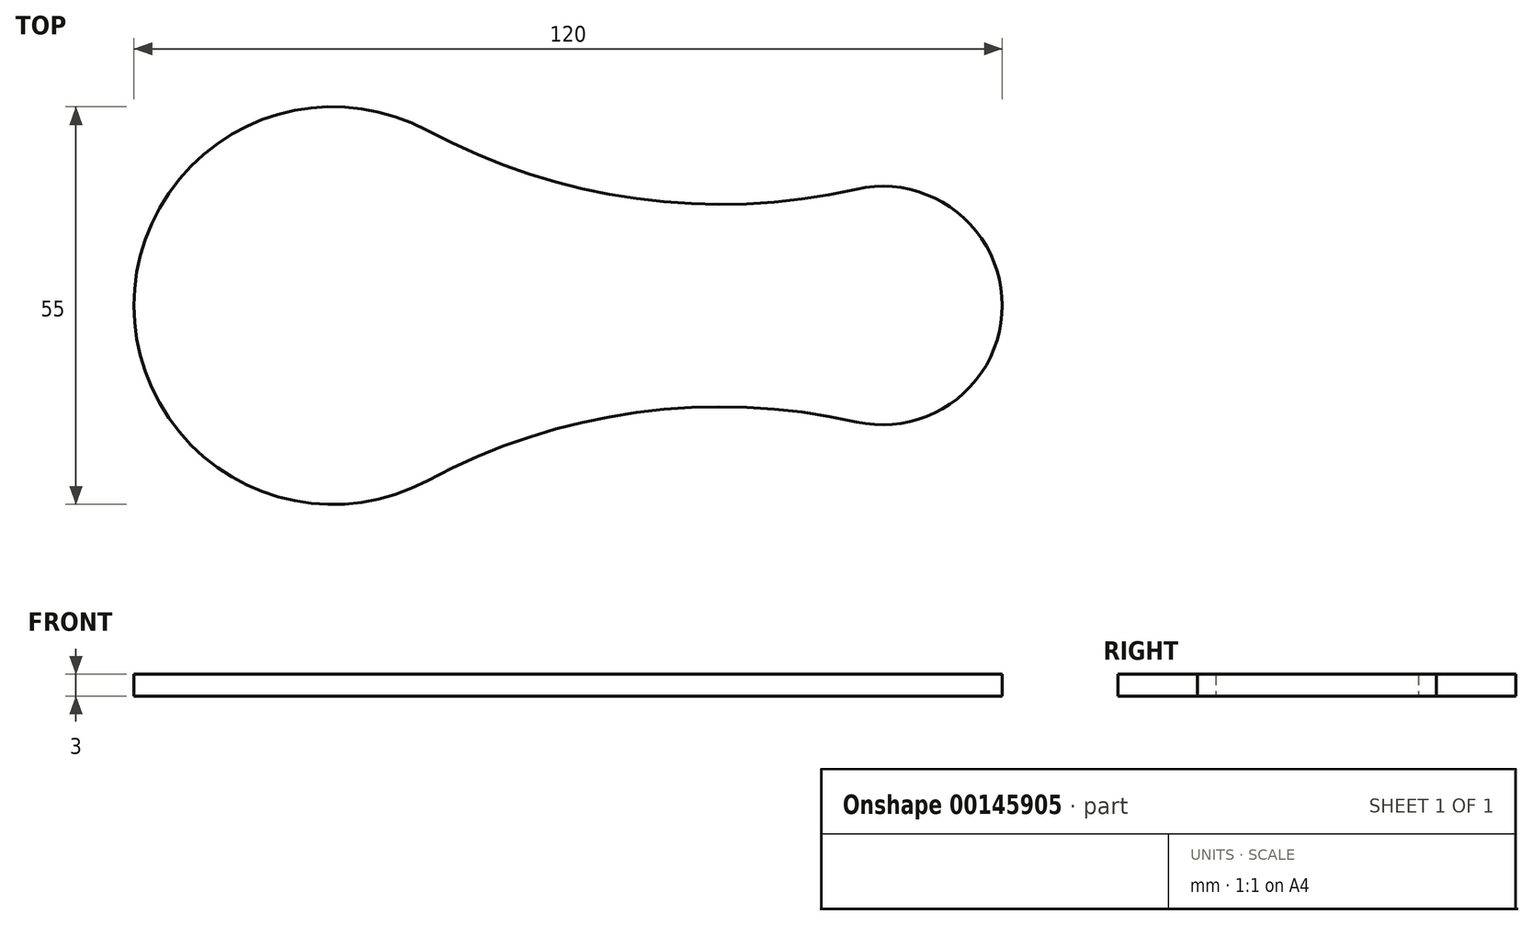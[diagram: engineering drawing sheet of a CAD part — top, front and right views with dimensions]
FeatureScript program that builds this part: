
annotation { "Feature Type Name" : "Feature", "Feature Type Description" : "" }
export const myFeature = defineFeature(function(context is Context, id is Id, definition is map)
    precondition{}
    {
        {
            var Q0;
            Q0=qCreatedBy(makeId("Top.planeOp"),FACE);
            var sketch = newSketch(context, id + "F0", { "sketchPlane" : qUnion([Q0])});
            skArc(sketch, "E0", {"start": v(72.37, 16.1) * mm, "mid": v(86.3, 12.89) * mm, "end": v(92.5, 0) * mm});
            skArc(sketch, "E1", {"start": v(13.04, 24.21) * mm, "mid": v(-14.1, 23.6) * mm, "end": v(-27.5, 0) * mm});
            skLineSegment(sketch, "E2", {"start": v(-27.5, 0) * mm, "end": v(92.5, 0) * mm, "construction": true});
            skArc(sketch, "E3", {"start": v(13.04, 24.21) * mm, "mid": v(41.97, 14.79) * mm, "end": v(72.37, 16.1) * mm});
            skArc(sketch, "E4.0", {"start": v(71.27, 20.97) * mm, "mid": v(89.43, 16.8) * mm, "end": v(97.5, 0) * mm});
            skArc(sketch, "E4.1", {"start": v(15.4, 28.62) * mm, "mid": v(42.65, 19.74) * mm, "end": v(71.27, 20.97) * mm});
            skArc(sketch, "E4.2", {"start": v(15.4, 28.62) * mm, "mid": v(-16.67, 27.9) * mm, "end": v(-32.5, 0) * mm});
            skArc(sketch, "E5.MirrorCS", {"start": v(13.04, -24.21) * mm, "mid": v(-14.1, -23.6) * mm, "end": v(-27.5, 0) * mm});
            skArc(sketch, "E6.MirrorCS", {"start": v(13.04, -24.21) * mm, "mid": v(41.97, -14.79) * mm, "end": v(72.37, -16.1) * mm});
            skArc(sketch, "E7.MirrorCS", {"start": v(71.27, -20.97) * mm, "mid": v(89.43, -16.8) * mm, "end": v(97.5, 0) * mm});
            skArc(sketch, "E8.MirrorCS", {"start": v(72.37, -16.1) * mm, "mid": v(86.3, -12.89) * mm, "end": v(92.5, 0) * mm});
            skArc(sketch, "E9.MirrorCS", {"start": v(15.4, -28.62) * mm, "mid": v(42.65, -19.74) * mm, "end": v(71.27, -20.97) * mm});
            skArc(sketch, "E10.MirrorCS", {"start": v(15.4, -28.62) * mm, "mid": v(-16.67, -27.9) * mm, "end": v(-32.5, 0) * mm});
            skSolve(sketch);
        }
        {
            var Q0;
            Q0=makeQuery(id+"F0.imprint","IMPRINT",FACE,{"disambiguationData":[TD([[makeQuery(id+"F0.imprint","IMPRINT",EDGE,{"derivedFrom":sQuery(id+"F0.wireOp",EDGE,"E0")}),1.0]])]});
            extrude(context, id + "F1", {"entities" : qUnion([Q0]), "depth" : 3 * mm});
        }
    });
